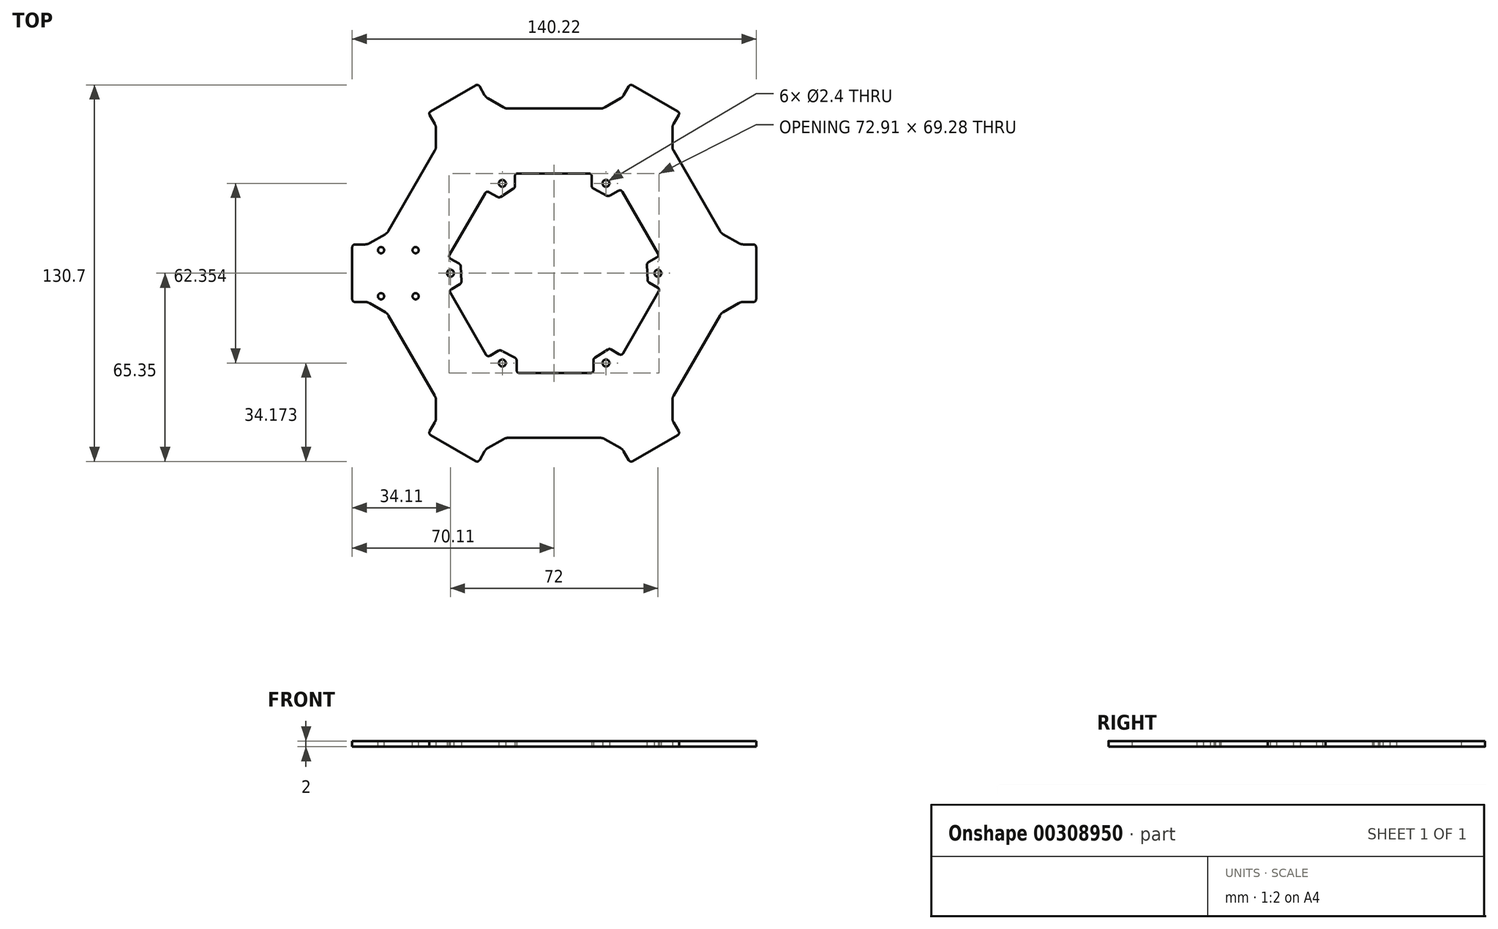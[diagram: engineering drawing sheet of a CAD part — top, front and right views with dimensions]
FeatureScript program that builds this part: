
annotation { "Feature Type Name" : "Feature", "Feature Type Description" : "" }
export const myFeature = defineFeature(function(context is Context, id is Id, definition is map)
    precondition{}
    {
        {
            var Q0;
            Q0=qCreatedBy(makeId("Top.planeOp"),FACE);
            var sketch = newSketch(context, id + "F0", { "sketchPlane" : qUnion([Q0])});
            skPoint(sketch, "E0.0.midPoint", {"position": v(0, 57.16) * mm});
            skLineSegment(sketch, "E1", {"start": v(-16.9, 57.16) * mm, "end": v(-23.73, 61.1) * mm});
            skLineSegment(sketch, "E2", {"start": v(-23.73, 61.1) * mm, "end": v(-26.4, 65.72) * mm});
            skLineSegment(sketch, "E3", {"start": v(-26.4, 65.72) * mm, "end": v(-43.71, 55.72) * mm});
            skLineSegment(sketch, "E4", {"start": v(-43.71, 55.72) * mm, "end": v(-41.05, 51.1) * mm});
            skLineSegment(sketch, "E5", {"start": v(-41.05, 51.1) * mm, "end": v(-41.05, 43.21) * mm});
            skLineSegment(sketch, "E6.1.0", {"start": v(43.71, 55.72) * mm, "end": v(26.4, 65.72) * mm});
            skLineSegment(sketch, "E6.1.1", {"start": v(41.05, 51.1) * mm, "end": v(43.71, 55.72) * mm});
            skLineSegment(sketch, "E6.1.2", {"start": v(41.05, 43.21) * mm, "end": v(41.05, 51.1) * mm});
            skLineSegment(sketch, "E6.1.3", {"start": v(26.4, 65.72) * mm, "end": v(23.73, 61.1) * mm});
            skLineSegment(sketch, "E6.1.4", {"start": v(23.73, 61.1) * mm, "end": v(16.9, 57.16) * mm});
            skLineSegment(sketch, "E6.2.0", {"start": v(70.1, -10) * mm, "end": v(70.1, 10) * mm});
            skLineSegment(sketch, "E6.2.1", {"start": v(64.78, -10) * mm, "end": v(70.1, -10) * mm});
            skLineSegment(sketch, "E6.2.2", {"start": v(57.95, -13.94) * mm, "end": v(64.78, -10) * mm});
            skLineSegment(sketch, "E6.2.3", {"start": v(70.1, 10) * mm, "end": v(64.78, 10) * mm});
            skLineSegment(sketch, "E6.2.4", {"start": v(64.78, 10) * mm, "end": v(57.95, 13.94) * mm});
            skPoint(sketch, "E6.center", {"position": v(0, 0) * mm});
            skLineSegment(sketch, "E7.2.3.0", {"start": v(26.4, -65.72) * mm, "end": v(43.71, -55.72) * mm});
            skLineSegment(sketch, "E7.3.3.0", {"start": v(23.73, -61.1) * mm, "end": v(26.4, -65.72) * mm});
            skLineSegment(sketch, "E7.6.3.0", {"start": v(16.9, -57.16) * mm, "end": v(23.73, -61.1) * mm});
            skLineSegment(sketch, "E7.9.3.0", {"start": v(43.71, -55.72) * mm, "end": v(41.05, -51.1) * mm});
            skLineSegment(sketch, "E7.12.3.0", {"start": v(41.05, -51.1) * mm, "end": v(41.05, -43.21) * mm});
            skLineSegment(sketch, "E7.2.4.0", {"start": v(-43.71, -55.72) * mm, "end": v(-26.4, -65.72) * mm});
            skLineSegment(sketch, "E7.3.4.0", {"start": v(-41.05, -51.1) * mm, "end": v(-43.71, -55.72) * mm});
            skLineSegment(sketch, "E7.6.4.0", {"start": v(-41.05, -43.21) * mm, "end": v(-41.05, -51.1) * mm});
            skLineSegment(sketch, "E7.9.4.0", {"start": v(-26.4, -65.72) * mm, "end": v(-23.73, -61.1) * mm});
            skLineSegment(sketch, "E7.12.4.0", {"start": v(-23.73, -61.1) * mm, "end": v(-16.9, -57.16) * mm});
            skLineSegment(sketch, "E7.2.5.0", {"start": v(-70.1, 10) * mm, "end": v(-70.1, -10) * mm});
            skLineSegment(sketch, "E7.3.5.0", {"start": v(-64.78, 10) * mm, "end": v(-70.1, 10) * mm});
            skLineSegment(sketch, "E7.6.5.0", {"start": v(-57.95, 13.94) * mm, "end": v(-64.78, 10) * mm});
            skLineSegment(sketch, "E7.9.5.0", {"start": v(-70.1, -10) * mm, "end": v(-64.78, -10) * mm});
            skLineSegment(sketch, "E7.12.5.0", {"start": v(-64.78, -10) * mm, "end": v(-57.95, -13.94) * mm});
            skLineSegment(sketch, "E8", {"start": v(16.9, 57.16) * mm, "end": v(-16.9, 57.16) * mm});
            skLineSegment(sketch, "E9", {"start": v(41.05, 43.21) * mm, "end": v(57.95, 13.94) * mm});
            skLineSegment(sketch, "E10", {"start": v(57.95, -13.94) * mm, "end": v(41.05, -43.21) * mm});
            skLineSegment(sketch, "E11", {"start": v(16.9, -57.16) * mm, "end": v(-16.9, -57.16) * mm});
            skLineSegment(sketch, "E12", {"start": v(-41.05, -43.21) * mm, "end": v(-57.95, -13.94) * mm});
            skLineSegment(sketch, "E13", {"start": v(-57.95, 13.94) * mm, "end": v(-41.05, 43.21) * mm});
            skLineSegment(sketch, "E14.0", {"start": v(-20, 34.64) * mm, "end": v(20, 34.64) * mm});
            skLineSegment(sketch, "E14.1", {"start": v(20, 34.64) * mm, "end": v(40, 0) * mm});
            skLineSegment(sketch, "E14.2", {"start": v(40, 0) * mm, "end": v(20, -34.64) * mm});
            skLineSegment(sketch, "E14.3", {"start": v(20, -34.64) * mm, "end": v(-20, -34.64) * mm});
            skLineSegment(sketch, "E14.4", {"start": v(-20, -34.64) * mm, "end": v(-40, 0) * mm});
            skLineSegment(sketch, "E14.5", {"start": v(-40, 0) * mm, "end": v(-20, 34.64) * mm});
            skPoint(sketch, "E14.0.midPoint", {"position": v(0, 34.64) * mm});
            skLineSegment(sketch, "E15", {"start": v(-13.65, 34.64) * mm, "end": v(-13.65, 29.64) * mm});
            skLineSegment(sketch, "E16", {"start": v(-13.65, 29.64) * mm, "end": v(-19.14, 26.13) * mm});
            skLineSegment(sketch, "E17", {"start": v(-19.14, 26.13) * mm, "end": v(-23.47, 28.63) * mm});
            skLineSegment(sketch, "E18.1.0", {"start": v(-32.2, -3.5) * mm, "end": v(-36.53, -6) * mm});
            skLineSegment(sketch, "E18.1.1", {"start": v(-32.5, 3) * mm, "end": v(-32.2, -3.5) * mm});
            skLineSegment(sketch, "E18.1.2", {"start": v(-36.82, 5.5) * mm, "end": v(-32.5, 3) * mm});
            skLineSegment(sketch, "E18.2.0", {"start": v(-13.06, -29.64) * mm, "end": v(-13.06, -34.64) * mm});
            skLineSegment(sketch, "E18.2.1", {"start": v(-18.85, -26.64) * mm, "end": v(-13.06, -29.64) * mm});
            skLineSegment(sketch, "E18.2.2", {"start": v(-23.18, -29.14) * mm, "end": v(-18.85, -26.64) * mm});
            skLineSegment(sketch, "E18.3.0", {"start": v(19.14, -26.13) * mm, "end": v(23.47, -28.63) * mm});
            skLineSegment(sketch, "E18.3.1", {"start": v(13.65, -29.64) * mm, "end": v(19.14, -26.13) * mm});
            skLineSegment(sketch, "E18.3.2", {"start": v(13.65, -34.64) * mm, "end": v(13.65, -29.64) * mm});
            skLineSegment(sketch, "E18.4.0", {"start": v(32.2, 3.5) * mm, "end": v(36.53, 6) * mm});
            skLineSegment(sketch, "E18.4.1", {"start": v(32.5, -3) * mm, "end": v(32.2, 3.5) * mm});
            skLineSegment(sketch, "E18.4.2", {"start": v(36.82, -5.5) * mm, "end": v(32.5, -3) * mm});
            skLineSegment(sketch, "E18.5.0", {"start": v(13.06, 29.64) * mm, "end": v(13.06, 34.64) * mm});
            skLineSegment(sketch, "E18.5.1", {"start": v(18.85, 26.64) * mm, "end": v(13.06, 29.64) * mm});
            skLineSegment(sketch, "E18.5.2", {"start": v(23.18, 29.14) * mm, "end": v(18.85, 26.64) * mm});
            skSolve(sketch);
        }
        {
            var Q0;
            Q0=makeQuery(id+"F0.imprint","IMPRINT",FACE,{"disambiguationData":[TD([[makeQuery(id+"F0.imprint","IMPRINT",EDGE,{"derivedFrom":sQuery(id+"F0.wireOp",EDGE,"E1")}),1.0]])]});
            var Q1;
            {var subQ0=sQuery(id+"F0.wireOp",EDGE,"E15");Q1=makeQuery(id+"F0.imprint","IMPRINT",FACE,{"disambiguationData":[TD([[makeQuery(id+"F0.imprint","IMPRINT",EDGE,{"derivedFrom":subQ0}),-1.0]])]});}
            var Q2;
            {var subQ0=sQuery(id+"F0.wireOp",EDGE,"E18.1.0");Q2=makeQuery(id+"F0.imprint","IMPRINT",FACE,{"disambiguationData":[TD([[makeQuery(id+"F0.imprint","IMPRINT",EDGE,{"derivedFrom":subQ0}),-1.0]])]});}
            var Q3;
            {var subQ0=sQuery(id+"F0.wireOp",EDGE,"E18.5.0");Q3=makeQuery(id+"F0.imprint","IMPRINT",FACE,{"disambiguationData":[TD([[makeQuery(id+"F0.imprint","IMPRINT",EDGE,{"derivedFrom":subQ0}),-1.0]])]});}
            var Q4;
            {var subQ4=sQuery(id+"F0.wireOp",EDGE,"E18.4.0");Q4=makeQuery(id+"F0.imprint","IMPRINT",FACE,{"disambiguationData":[TD([[makeQuery(id+"F0.imprint","IMPRINT",EDGE,{"derivedFrom":subQ4}),-1.0]])]});}
            var Q5;
            {var subQ0=sQuery(id+"F0.wireOp",EDGE,"E18.3.0");Q5=makeQuery(id+"F0.imprint","IMPRINT",FACE,{"disambiguationData":[TD([[makeQuery(id+"F0.imprint","IMPRINT",EDGE,{"derivedFrom":subQ0}),-1.0]])]});}
            var Q6;
            {var subQ0=sQuery(id+"F0.wireOp",EDGE,"E18.2.0");Q6=makeQuery(id+"F0.imprint","IMPRINT",FACE,{"disambiguationData":[TD([[makeQuery(id+"F0.imprint","IMPRINT",EDGE,{"derivedFrom":subQ0}),-1.0]])]});}
            extrude(context, id + "F1", {"entities" : qUnion([Q0, Q1, Q2, Q3, Q4, Q5, Q6]), "offsetDistance" : 25 * mm, "depth" : 2 * mm});
        }
        {
            var Q0;
            Q0=qCreatedBy(makeId("Top.planeOp"),FACE);
            var sketch = newSketch(context, id + "F2", { "sketchPlane" : qUnion([Q0])});
            skCircle(sketch, "E19.cCircle", {"center": v(0, 0) * mm, "radius": 31.18 * mm, "construction": true});
            skLineSegment(sketch, "E19.0", {"start": v(-18, 31.18) * mm, "end": v(18, 31.18) * mm});
            skLineSegment(sketch, "E19.1", {"start": v(18, 31.18) * mm, "end": v(36, 0) * mm});
            skLineSegment(sketch, "E19.2", {"start": v(36, 0) * mm, "end": v(18, -31.18) * mm});
            skLineSegment(sketch, "E19.3", {"start": v(18, -31.18) * mm, "end": v(-18, -31.18) * mm});
            skLineSegment(sketch, "E19.4", {"start": v(-18, -31.18) * mm, "end": v(-36, 0) * mm});
            skLineSegment(sketch, "E19.5", {"start": v(-36, 0) * mm, "end": v(-18, 31.18) * mm});
            skPoint(sketch, "E19.0.midPoint", {"position": v(0, 31.18) * mm});
            skSolve(sketch);
        }
        {
            var Q0;
            Q0=sQuery(id+"F2.wireOp",VERTEX,"E19.5.start");
            var Q1;
            Q1=sQuery(id+"F2.wireOp",VERTEX,"E19.0.start");
            var Q2;
            Q2=sQuery(id+"F2.wireOp",VERTEX,"E19.1.start");
            var Q3;
            Q3=sQuery(id+"F2.wireOp",VERTEX,"E19.2.start");
            var Q4;
            Q4=sQuery(id+"F2.wireOp",VERTEX,"E19.3.start");
            var Q5;
            Q5=sQuery(id+"F2.wireOp",VERTEX,"E19.4.start");
            var Q6;
            Q6=makeQuery(id+"F1.opExtrude","SWEPT_BODY",BODY,{"disambiguationData":[OSD([sQuery(id+"F0.wireOp",EDGE,"E1"),sQuery(id+"F0.wireOp",EDGE,"E2"),sQuery(id+"F0.wireOp",EDGE,"E3"),sQuery(id+"F0.wireOp",EDGE,"E4"),sQuery(id+"F0.wireOp",EDGE,"E5"),sQuery(id+"F0.wireOp",EDGE,"E6.1.0"),sQuery(id+"F0.wireOp",EDGE,"E6.1.1"),sQuery(id+"F0.wireOp",EDGE,"E6.1.2"),sQuery(id+"F0.wireOp",EDGE,"E6.1.3"),sQuery(id+"F0.wireOp",EDGE,"E6.1.4"),sQuery(id+"F0.wireOp",EDGE,"E6.2.0"),sQuery(id+"F0.wireOp",EDGE,"E6.2.1"),sQuery(id+"F0.wireOp",EDGE,"E6.2.2"),sQuery(id+"F0.wireOp",EDGE,"E6.2.3"),sQuery(id+"F0.wireOp",EDGE,"E6.2.4"),sQuery(id+"F0.wireOp",EDGE,"E7.2.3.0"),sQuery(id+"F0.wireOp",EDGE,"E7.3.3.0"),sQuery(id+"F0.wireOp",EDGE,"E7.6.3.0"),sQuery(id+"F0.wireOp",EDGE,"E7.9.3.0"),sQuery(id+"F0.wireOp",EDGE,"E7.12.3.0"),sQuery(id+"F0.wireOp",EDGE,"E7.2.4.0"),sQuery(id+"F0.wireOp",EDGE,"E7.3.4.0"),sQuery(id+"F0.wireOp",EDGE,"E7.6.4.0"),sQuery(id+"F0.wireOp",EDGE,"E7.9.4.0"),sQuery(id+"F0.wireOp",EDGE,"E7.12.4.0"),sQuery(id+"F0.wireOp",EDGE,"E7.2.5.0"),sQuery(id+"F0.wireOp",EDGE,"E7.3.5.0"),sQuery(id+"F0.wireOp",EDGE,"E7.6.5.0"),sQuery(id+"F0.wireOp",EDGE,"E7.9.5.0"),sQuery(id+"F0.wireOp",EDGE,"E7.12.5.0"),sQuery(id+"F0.wireOp",EDGE,"E8"),sQuery(id+"F0.wireOp",EDGE,"E9"),sQuery(id+"F0.wireOp",EDGE,"E10"),sQuery(id+"F0.wireOp",EDGE,"E11"),sQuery(id+"F0.wireOp",EDGE,"E12"),sQuery(id+"F0.wireOp",EDGE,"E13"),sQuery(id+"F0.wireOp",EDGE,"E14.0"),sQuery(id+"F0.wireOp",EDGE,"E14.1"),sQuery(id+"F0.wireOp",EDGE,"E14.2"),sQuery(id+"F0.wireOp",EDGE,"E14.3"),sQuery(id+"F0.wireOp",EDGE,"E14.4"),sQuery(id+"F0.wireOp",EDGE,"E14.5"),sQuery(id+"F0.wireOp",EDGE,"E15"),sQuery(id+"F0.wireOp",EDGE,"E16"),sQuery(id+"F0.wireOp",EDGE,"E17"),sQuery(id+"F0.wireOp",EDGE,"E18.1.0"),sQuery(id+"F0.wireOp",EDGE,"E18.1.1"),sQuery(id+"F0.wireOp",EDGE,"E18.1.2"),sQuery(id+"F0.wireOp",EDGE,"E18.2.0"),sQuery(id+"F0.wireOp",EDGE,"E18.2.1"),sQuery(id+"F0.wireOp",EDGE,"E18.2.2"),sQuery(id+"F0.wireOp",EDGE,"E18.3.0"),sQuery(id+"F0.wireOp",EDGE,"E18.3.1"),sQuery(id+"F0.wireOp",EDGE,"E18.3.2"),sQuery(id+"F0.wireOp",EDGE,"E18.4.0"),sQuery(id+"F0.wireOp",EDGE,"E18.4.1"),sQuery(id+"F0.wireOp",EDGE,"E18.4.2"),sQuery(id+"F0.wireOp",EDGE,"E18.5.0"),sQuery(id+"F0.wireOp",EDGE,"E18.5.1"),sQuery(id+"F0.wireOp",EDGE,"E18.5.2")])]});
            hole(context, id + "F3", {"style" : HoleStyle.SIMPLE, "endStyle" : HoleEndStyle.THROUGH, "oppositeDirection" : true, "standardTappedOrClearance" : lookupTablePath({ "standard" : "ISO", "engagement" : "75%", "pitch" : "0.6 mm", "size" : "M3", "type" : "Tapped" }), "standardBlindInLast" : lookupTablePath({ "standard" : "ISO", "engagement" : "75%", "pitch" : "0.6 mm", "size" : "M3", "type" : "Tapped" }), "holeDiameter" : 2.4 * mm, "majorDiameter" : 5 * mm, "showTappedDepth" : true, "tappedDepth" : 12 * mm, "tapClearance" : 3, "locations" : qUnion([Q0, Q1, Q2, Q3, Q4, Q5]), "scope" : qUnion([Q6])});
        }
        {
            var Q0;
            Q0=makeQuery(id+"F1.opExtrude","SWEPT_EDGE",EDGE,{"disambiguationData":[OSD([sQuery(id+"F0.wireOp",EDGE,"E7.2.4.0"),sQuery(id+"F0.wireOp",EDGE,"E7.9.4.0")])]});
            var Q1;
            Q1=makeQuery(id+"F1.opExtrude","SWEPT_EDGE",EDGE,{"disambiguationData":[OSD([sQuery(id+"F0.wireOp",EDGE,"E7.2.4.0"),sQuery(id+"F0.wireOp",EDGE,"E7.3.4.0")])]});
            var Q2;
            Q2=makeQuery(id+"F1.opExtrude","SWEPT_EDGE",EDGE,{"disambiguationData":[OSD([sQuery(id+"F0.wireOp",EDGE,"E7.2.3.0"),sQuery(id+"F0.wireOp",EDGE,"E7.3.3.0")])]});
            var Q3;
            Q3=makeQuery(id+"F1.opExtrude","SWEPT_EDGE",EDGE,{"disambiguationData":[OSD([sQuery(id+"F0.wireOp",EDGE,"E7.2.3.0"),sQuery(id+"F0.wireOp",EDGE,"E7.9.3.0")])]});
            var Q4;
            Q4=makeQuery(id+"F1.opExtrude","SWEPT_EDGE",EDGE,{"disambiguationData":[OSD([sQuery(id+"F0.wireOp",EDGE,"E6.2.0"),sQuery(id+"F0.wireOp",EDGE,"E6.2.1")])]});
            var Q5;
            Q5=makeQuery(id+"F1.opExtrude","SWEPT_EDGE",EDGE,{"disambiguationData":[OSD([sQuery(id+"F0.wireOp",EDGE,"E6.2.0"),sQuery(id+"F0.wireOp",EDGE,"E6.2.3")])]});
            var Q6;
            Q6=makeQuery(id+"F1.opExtrude","SWEPT_EDGE",EDGE,{"disambiguationData":[OSD([sQuery(id+"F0.wireOp",EDGE,"E6.1.0"),sQuery(id+"F0.wireOp",EDGE,"E6.1.3")])]});
            var Q7;
            Q7=makeQuery(id+"F1.opExtrude","SWEPT_EDGE",EDGE,{"disambiguationData":[OSD([sQuery(id+"F0.wireOp",EDGE,"E6.1.0"),sQuery(id+"F0.wireOp",EDGE,"E6.1.1")])]});
            var Q8;
            Q8=makeQuery(id+"F1.opExtrude","SWEPT_EDGE",EDGE,{"disambiguationData":[OSD([sQuery(id+"F0.wireOp",EDGE,"E2"),sQuery(id+"F0.wireOp",EDGE,"E3")])]});
            var Q9;
            Q9=makeQuery(id+"F1.opExtrude","SWEPT_EDGE",EDGE,{"disambiguationData":[OSD([sQuery(id+"F0.wireOp",EDGE,"E3"),sQuery(id+"F0.wireOp",EDGE,"E4")])]});
            var Q10;
            Q10=makeQuery(id+"F1.opExtrude","SWEPT_EDGE",EDGE,{"disambiguationData":[OSD([sQuery(id+"F0.wireOp",EDGE,"E7.2.5.0"),sQuery(id+"F0.wireOp",EDGE,"E7.3.5.0")])]});
            var Q11;
            Q11=makeQuery(id+"F1.opExtrude","SWEPT_EDGE",EDGE,{"disambiguationData":[OSD([sQuery(id+"F0.wireOp",EDGE,"E7.2.5.0"),sQuery(id+"F0.wireOp",EDGE,"E7.9.5.0")])]});
            var Q12;
            Q12=makeQuery(id+"F1.opExtrude","SWEPT_EDGE",EDGE,{"disambiguationData":[OSD([sQuery(id+"F0.wireOp",EDGE,"E18.4.0"),sQuery(id+"F0.wireOp",EDGE,"E18.4.1")])]});
            var Q13;
            Q13=makeQuery(id+"F1.opExtrude","SWEPT_EDGE",EDGE,{"disambiguationData":[OSD([sQuery(id+"F0.wireOp",EDGE,"E18.4.1"),sQuery(id+"F0.wireOp",EDGE,"E18.4.2")])]});
            var Q14;
            Q14=makeQuery(id+"F1.opExtrude","SWEPT_EDGE",EDGE,{"disambiguationData":[OSD([sQuery(id+"F0.wireOp",EDGE,"E18.3.1"),sQuery(id+"F0.wireOp",EDGE,"E18.3.2")])]});
            var Q15;
            Q15=makeQuery(id+"F1.opExtrude","SWEPT_EDGE",EDGE,{"disambiguationData":[OSD([sQuery(id+"F0.wireOp",EDGE,"E18.3.0"),sQuery(id+"F0.wireOp",EDGE,"E18.3.1")])]});
            var Q16;
            Q16=makeQuery(id+"F1.opExtrude","SWEPT_EDGE",EDGE,{"disambiguationData":[OSD([sQuery(id+"F0.wireOp",EDGE,"E18.2.1"),sQuery(id+"F0.wireOp",EDGE,"E18.2.2")])]});
            var Q17;
            Q17=makeQuery(id+"F1.opExtrude","SWEPT_EDGE",EDGE,{"disambiguationData":[OSD([sQuery(id+"F0.wireOp",EDGE,"E18.2.0"),sQuery(id+"F0.wireOp",EDGE,"E18.2.1")])]});
            var Q18;
            Q18=makeQuery(id+"F1.opExtrude","SWEPT_EDGE",EDGE,{"disambiguationData":[OSD([sQuery(id+"F0.wireOp",EDGE,"E18.1.1"),sQuery(id+"F0.wireOp",EDGE,"E18.1.2")])]});
            var Q19;
            Q19=makeQuery(id+"F1.opExtrude","SWEPT_EDGE",EDGE,{"disambiguationData":[OSD([sQuery(id+"F0.wireOp",EDGE,"E18.1.0"),sQuery(id+"F0.wireOp",EDGE,"E18.1.1")])]});
            var Q20;
            Q20=makeQuery(id+"F1.opExtrude","SWEPT_EDGE",EDGE,{"disambiguationData":[OSD([sQuery(id+"F0.wireOp",EDGE,"E16"),sQuery(id+"F0.wireOp",EDGE,"E17")])]});
            var Q21;
            Q21=makeQuery(id+"F1.opExtrude","SWEPT_EDGE",EDGE,{"disambiguationData":[OSD([sQuery(id+"F0.wireOp",EDGE,"E15"),sQuery(id+"F0.wireOp",EDGE,"E16")])]});
            var Q22;
            Q22=makeQuery(id+"F1.opExtrude","SWEPT_EDGE",EDGE,{"disambiguationData":[OSD([sQuery(id+"F0.wireOp",EDGE,"E18.5.0"),sQuery(id+"F0.wireOp",EDGE,"E18.5.1")])]});
            var Q23;
            Q23=makeQuery(id+"F1.opExtrude","SWEPT_EDGE",EDGE,{"disambiguationData":[OSD([sQuery(id+"F0.wireOp",EDGE,"E18.5.1"),sQuery(id+"F0.wireOp",EDGE,"E18.5.2")])]});
            var Q24;
            Q24=makeQuery(id+"F1.opExtrude","SWEPT_EDGE",EDGE,{"disambiguationData":[OSD([sQuery(id+"F0.wireOp",EDGE,"E14.1"),sQuery(id+"F0.wireOp",EDGE,"E18.5.2")])]});
            var Q25;
            Q25=makeQuery(id+"F1.opExtrude","SWEPT_EDGE",EDGE,{"disambiguationData":[OSD([sQuery(id+"F0.wireOp",EDGE,"E14.0"),sQuery(id+"F0.wireOp",EDGE,"E18.5.0")])]});
            var Q26;
            Q26=makeQuery(id+"F1.opExtrude","SWEPT_EDGE",EDGE,{"disambiguationData":[OSD([sQuery(id+"F0.wireOp",EDGE,"E14.2"),sQuery(id+"F0.wireOp",EDGE,"E18.4.2")])]});
            var Q27;
            Q27=makeQuery(id+"F1.opExtrude","SWEPT_EDGE",EDGE,{"disambiguationData":[OSD([sQuery(id+"F0.wireOp",EDGE,"E14.1"),sQuery(id+"F0.wireOp",EDGE,"E18.4.0")])]});
            var Q28;
            Q28=makeQuery(id+"F1.opExtrude","SWEPT_EDGE",EDGE,{"disambiguationData":[OSD([sQuery(id+"F0.wireOp",EDGE,"E14.2"),sQuery(id+"F0.wireOp",EDGE,"E18.3.0")])]});
            var Q29;
            Q29=makeQuery(id+"F1.opExtrude","SWEPT_EDGE",EDGE,{"disambiguationData":[OSD([sQuery(id+"F0.wireOp",EDGE,"E14.3"),sQuery(id+"F0.wireOp",EDGE,"E18.3.2")])]});
            var Q30;
            Q30=makeQuery(id+"F1.opExtrude","SWEPT_EDGE",EDGE,{"disambiguationData":[OSD([sQuery(id+"F0.wireOp",EDGE,"E14.3"),sQuery(id+"F0.wireOp",EDGE,"E18.2.0")])]});
            var Q31;
            Q31=makeQuery(id+"F1.opExtrude","SWEPT_EDGE",EDGE,{"disambiguationData":[OSD([sQuery(id+"F0.wireOp",EDGE,"E14.5"),sQuery(id+"F0.wireOp",EDGE,"E18.1.2")])]});
            var Q32;
            Q32=makeQuery(id+"F1.opExtrude","SWEPT_EDGE",EDGE,{"disambiguationData":[OSD([sQuery(id+"F0.wireOp",EDGE,"E14.4"),sQuery(id+"F0.wireOp",EDGE,"E18.1.0")])]});
            var Q33;
            Q33=makeQuery(id+"F1.opExtrude","SWEPT_EDGE",EDGE,{"disambiguationData":[OSD([sQuery(id+"F0.wireOp",EDGE,"E14.4"),sQuery(id+"F0.wireOp",EDGE,"E18.2.2")])]});
            var Q34;
            Q34=makeQuery(id+"F1.opExtrude","SWEPT_EDGE",EDGE,{"disambiguationData":[OSD([sQuery(id+"F0.wireOp",EDGE,"E14.0"),sQuery(id+"F0.wireOp",EDGE,"E15")])]});
            var Q35;
            Q35=makeQuery(id+"F1.opExtrude","SWEPT_EDGE",EDGE,{"disambiguationData":[OSD([sQuery(id+"F0.wireOp",EDGE,"E14.5"),sQuery(id+"F0.wireOp",EDGE,"E17")])]});
            fillet(context, id + "F4", {"entities" : qUnion([Q0, Q1, Q2, Q3, Q4, Q5, Q6, Q7, Q8, Q9, Q10, Q11, Q12, Q13, Q14, Q15, Q16, Q17, Q18, Q19, Q20, Q21, Q22, Q23, Q24, Q25, Q26, Q27, Q28, Q29, Q30, Q31, Q32, Q33, Q34, Q35]), "radius" : 1 * mm, "tangentPropagation" : true, "allowEdgeOverflow" : false});
        }
        {
            var Q0;
            Q0=makeQuery(id+"F1.opExtrude","SWEPT_EDGE",EDGE,{"disambiguationData":[OSD([sQuery(id+"F0.wireOp",EDGE,"E7.9.5.0"),sQuery(id+"F0.wireOp",EDGE,"E7.12.5.0")])]});
            var Q1;
            Q1=makeQuery(id+"F1.opExtrude","SWEPT_EDGE",EDGE,{"disambiguationData":[OSD([sQuery(id+"F0.wireOp",EDGE,"E7.12.5.0"),sQuery(id+"F0.wireOp",EDGE,"E12")])]});
            var Q2;
            Q2=makeQuery(id+"F1.opExtrude","SWEPT_EDGE",EDGE,{"disambiguationData":[OSD([sQuery(id+"F0.wireOp",EDGE,"E7.6.4.0"),sQuery(id+"F0.wireOp",EDGE,"E12")])]});
            var Q3;
            Q3=makeQuery(id+"F1.opExtrude","SWEPT_EDGE",EDGE,{"disambiguationData":[OSD([sQuery(id+"F0.wireOp",EDGE,"E7.3.4.0"),sQuery(id+"F0.wireOp",EDGE,"E7.6.4.0")])]});
            var Q4;
            Q4=makeQuery(id+"F1.opExtrude","SWEPT_EDGE",EDGE,{"disambiguationData":[OSD([sQuery(id+"F0.wireOp",EDGE,"E7.12.4.0"),sQuery(id+"F0.wireOp",EDGE,"E11")])]});
            var Q5;
            Q5=makeQuery(id+"F1.opExtrude","SWEPT_EDGE",EDGE,{"disambiguationData":[OSD([sQuery(id+"F0.wireOp",EDGE,"E7.9.4.0"),sQuery(id+"F0.wireOp",EDGE,"E7.12.4.0")])]});
            var Q6;
            Q6=makeQuery(id+"F1.opExtrude","SWEPT_EDGE",EDGE,{"disambiguationData":[OSD([sQuery(id+"F0.wireOp",EDGE,"E7.6.3.0"),sQuery(id+"F0.wireOp",EDGE,"E11")])]});
            var Q7;
            Q7=makeQuery(id+"F1.opExtrude","SWEPT_EDGE",EDGE,{"disambiguationData":[OSD([sQuery(id+"F0.wireOp",EDGE,"E7.3.3.0"),sQuery(id+"F0.wireOp",EDGE,"E7.6.3.0")])]});
            var Q8;
            Q8=makeQuery(id+"F1.opExtrude","SWEPT_EDGE",EDGE,{"disambiguationData":[OSD([sQuery(id+"F0.wireOp",EDGE,"E7.9.3.0"),sQuery(id+"F0.wireOp",EDGE,"E7.12.3.0")])]});
            var Q9;
            Q9=makeQuery(id+"F1.opExtrude","SWEPT_EDGE",EDGE,{"disambiguationData":[OSD([sQuery(id+"F0.wireOp",EDGE,"E7.12.3.0"),sQuery(id+"F0.wireOp",EDGE,"E10")])]});
            var Q10;
            Q10=makeQuery(id+"F1.opExtrude","SWEPT_EDGE",EDGE,{"disambiguationData":[OSD([sQuery(id+"F0.wireOp",EDGE,"E6.2.2"),sQuery(id+"F0.wireOp",EDGE,"E10")])]});
            var Q11;
            Q11=makeQuery(id+"F1.opExtrude","SWEPT_EDGE",EDGE,{"disambiguationData":[OSD([sQuery(id+"F0.wireOp",EDGE,"E6.2.1"),sQuery(id+"F0.wireOp",EDGE,"E6.2.2")])]});
            var Q12;
            Q12=makeQuery(id+"F1.opExtrude","SWEPT_EDGE",EDGE,{"disambiguationData":[OSD([sQuery(id+"F0.wireOp",EDGE,"E6.2.4"),sQuery(id+"F0.wireOp",EDGE,"E9")])]});
            var Q13;
            Q13=makeQuery(id+"F1.opExtrude","SWEPT_EDGE",EDGE,{"disambiguationData":[OSD([sQuery(id+"F0.wireOp",EDGE,"E6.2.3"),sQuery(id+"F0.wireOp",EDGE,"E6.2.4")])]});
            var Q14;
            Q14=makeQuery(id+"F1.opExtrude","SWEPT_EDGE",EDGE,{"disambiguationData":[OSD([sQuery(id+"F0.wireOp",EDGE,"E6.1.1"),sQuery(id+"F0.wireOp",EDGE,"E6.1.2")])]});
            var Q15;
            Q15=makeQuery(id+"F1.opExtrude","SWEPT_EDGE",EDGE,{"disambiguationData":[OSD([sQuery(id+"F0.wireOp",EDGE,"E6.1.2"),sQuery(id+"F0.wireOp",EDGE,"E9")])]});
            var Q16;
            Q16=makeQuery(id+"F1.opExtrude","SWEPT_EDGE",EDGE,{"disambiguationData":[OSD([sQuery(id+"F0.wireOp",EDGE,"E6.1.3"),sQuery(id+"F0.wireOp",EDGE,"E6.1.4")])]});
            var Q17;
            Q17=makeQuery(id+"F1.opExtrude","SWEPT_EDGE",EDGE,{"disambiguationData":[OSD([sQuery(id+"F0.wireOp",EDGE,"E6.1.4"),sQuery(id+"F0.wireOp",EDGE,"E8")])]});
            var Q18;
            Q18=makeQuery(id+"F1.opExtrude","SWEPT_EDGE",EDGE,{"disambiguationData":[OSD([sQuery(id+"F0.wireOp",EDGE,"E1"),sQuery(id+"F0.wireOp",EDGE,"E8")])]});
            var Q19;
            Q19=makeQuery(id+"F1.opExtrude","SWEPT_EDGE",EDGE,{"disambiguationData":[OSD([sQuery(id+"F0.wireOp",EDGE,"E1"),sQuery(id+"F0.wireOp",EDGE,"E2")])]});
            var Q20;
            Q20=makeQuery(id+"F1.opExtrude","SWEPT_EDGE",EDGE,{"disambiguationData":[OSD([sQuery(id+"F0.wireOp",EDGE,"E5"),sQuery(id+"F0.wireOp",EDGE,"E13")])]});
            var Q21;
            Q21=makeQuery(id+"F1.opExtrude","SWEPT_EDGE",EDGE,{"disambiguationData":[OSD([sQuery(id+"F0.wireOp",EDGE,"E4"),sQuery(id+"F0.wireOp",EDGE,"E5")])]});
            var Q22;
            Q22=makeQuery(id+"F1.opExtrude","SWEPT_EDGE",EDGE,{"disambiguationData":[OSD([sQuery(id+"F0.wireOp",EDGE,"E7.3.5.0"),sQuery(id+"F0.wireOp",EDGE,"E7.6.5.0")])]});
            var Q23;
            Q23=makeQuery(id+"F1.opExtrude","SWEPT_EDGE",EDGE,{"disambiguationData":[OSD([sQuery(id+"F0.wireOp",EDGE,"E7.6.5.0"),sQuery(id+"F0.wireOp",EDGE,"E13")])]});
            fillet(context, id + "F5", {"entities" : qUnion([Q0, Q1, Q2, Q3, Q4, Q5, Q6, Q7, Q8, Q9, Q10, Q11, Q12, Q13, Q14, Q15, Q16, Q17, Q18, Q19, Q20, Q21, Q22, Q23]), "radius" : 3 * mm, "tangentPropagation" : true, "allowEdgeOverflow" : false});
        }
        {
            var Q0;
            Q0=makeQuery(id+"F1.opExtrude","CAP_FACE",FACE,{"disambiguationData":[OSD([sQuery(id+"F0.wireOp",EDGE,"E1"),sQuery(id+"F0.wireOp",EDGE,"E2"),sQuery(id+"F0.wireOp",EDGE,"E3"),sQuery(id+"F0.wireOp",EDGE,"E4"),sQuery(id+"F0.wireOp",EDGE,"E5"),sQuery(id+"F0.wireOp",EDGE,"E6.1.0"),sQuery(id+"F0.wireOp",EDGE,"E6.1.1"),sQuery(id+"F0.wireOp",EDGE,"E6.1.2"),sQuery(id+"F0.wireOp",EDGE,"E6.1.3"),sQuery(id+"F0.wireOp",EDGE,"E6.1.4"),sQuery(id+"F0.wireOp",EDGE,"E6.2.0"),sQuery(id+"F0.wireOp",EDGE,"E6.2.1"),sQuery(id+"F0.wireOp",EDGE,"E6.2.2"),sQuery(id+"F0.wireOp",EDGE,"E6.2.3"),sQuery(id+"F0.wireOp",EDGE,"E6.2.4"),sQuery(id+"F0.wireOp",EDGE,"E7.2.3.0"),sQuery(id+"F0.wireOp",EDGE,"E7.3.3.0"),sQuery(id+"F0.wireOp",EDGE,"E7.6.3.0"),sQuery(id+"F0.wireOp",EDGE,"E7.9.3.0"),sQuery(id+"F0.wireOp",EDGE,"E7.12.3.0"),sQuery(id+"F0.wireOp",EDGE,"E7.2.4.0"),sQuery(id+"F0.wireOp",EDGE,"E7.3.4.0"),sQuery(id+"F0.wireOp",EDGE,"E7.6.4.0"),sQuery(id+"F0.wireOp",EDGE,"E7.9.4.0"),sQuery(id+"F0.wireOp",EDGE,"E7.12.4.0"),sQuery(id+"F0.wireOp",EDGE,"E7.2.5.0"),sQuery(id+"F0.wireOp",EDGE,"E7.3.5.0"),sQuery(id+"F0.wireOp",EDGE,"E7.6.5.0"),sQuery(id+"F0.wireOp",EDGE,"E7.9.5.0"),sQuery(id+"F0.wireOp",EDGE,"E7.12.5.0"),sQuery(id+"F0.wireOp",EDGE,"E8"),sQuery(id+"F0.wireOp",EDGE,"E9"),sQuery(id+"F0.wireOp",EDGE,"E10"),sQuery(id+"F0.wireOp",EDGE,"E11"),sQuery(id+"F0.wireOp",EDGE,"E12"),sQuery(id+"F0.wireOp",EDGE,"E13"),sQuery(id+"F0.wireOp",EDGE,"E14.0"),sQuery(id+"F0.wireOp",EDGE,"E14.1"),sQuery(id+"F0.wireOp",EDGE,"E14.2"),sQuery(id+"F0.wireOp",EDGE,"E14.3"),sQuery(id+"F0.wireOp",EDGE,"E14.4"),sQuery(id+"F0.wireOp",EDGE,"E14.5"),sQuery(id+"F0.wireOp",EDGE,"E15"),sQuery(id+"F0.wireOp",EDGE,"E16"),sQuery(id+"F0.wireOp",EDGE,"E17"),sQuery(id+"F0.wireOp",EDGE,"E18.1.0"),sQuery(id+"F0.wireOp",EDGE,"E18.1.1"),sQuery(id+"F0.wireOp",EDGE,"E18.1.2"),sQuery(id+"F0.wireOp",EDGE,"E18.2.0"),sQuery(id+"F0.wireOp",EDGE,"E18.2.1"),sQuery(id+"F0.wireOp",EDGE,"E18.2.2"),sQuery(id+"F0.wireOp",EDGE,"E18.3.0"),sQuery(id+"F0.wireOp",EDGE,"E18.3.1"),sQuery(id+"F0.wireOp",EDGE,"E18.3.2"),sQuery(id+"F0.wireOp",EDGE,"E18.4.0"),sQuery(id+"F0.wireOp",EDGE,"E18.4.1"),sQuery(id+"F0.wireOp",EDGE,"E18.4.2"),sQuery(id+"F0.wireOp",EDGE,"E18.5.0"),sQuery(id+"F0.wireOp",EDGE,"E18.5.1"),sQuery(id+"F0.wireOp",EDGE,"E18.5.2")])],"isStart":false});
            var sketch = newSketch(context, id + "F6", { "sketchPlane" : qUnion([Q0])});
            skLineSegment(sketch, "E20", {"start": v(-60.1, 8) * mm, "end": v(-60.1, -8) * mm});
            skLineSegment(sketch, "E21", {"start": v(-48.1, 8) * mm, "end": v(-48.1, -8) * mm});
            skSolve(sketch);
        }
        {
            var Q0;
            Q0=sQuery(id+"F6.wireOp",VERTEX,"E21.start");
            var Q1;
            Q1=sQuery(id+"F6.wireOp",VERTEX,"E21.end");
            var Q2;
            Q2=sQuery(id+"F6.wireOp",VERTEX,"E20.end");
            var Q3;
            Q3=sQuery(id+"F6.wireOp",VERTEX,"E20.start");
            var Q4;
            Q4=makeQuery(id+"F1.opExtrude","SWEPT_BODY",BODY,{"disambiguationData":[OSD([sQuery(id+"F0.wireOp",EDGE,"E1"),sQuery(id+"F0.wireOp",EDGE,"E2"),sQuery(id+"F0.wireOp",EDGE,"E3"),sQuery(id+"F0.wireOp",EDGE,"E4"),sQuery(id+"F0.wireOp",EDGE,"E5"),sQuery(id+"F0.wireOp",EDGE,"E6.1.0"),sQuery(id+"F0.wireOp",EDGE,"E6.1.1"),sQuery(id+"F0.wireOp",EDGE,"E6.1.2"),sQuery(id+"F0.wireOp",EDGE,"E6.1.3"),sQuery(id+"F0.wireOp",EDGE,"E6.1.4"),sQuery(id+"F0.wireOp",EDGE,"E6.2.0"),sQuery(id+"F0.wireOp",EDGE,"E6.2.1"),sQuery(id+"F0.wireOp",EDGE,"E6.2.2"),sQuery(id+"F0.wireOp",EDGE,"E6.2.3"),sQuery(id+"F0.wireOp",EDGE,"E6.2.4"),sQuery(id+"F0.wireOp",EDGE,"E7.2.3.0"),sQuery(id+"F0.wireOp",EDGE,"E7.3.3.0"),sQuery(id+"F0.wireOp",EDGE,"E7.6.3.0"),sQuery(id+"F0.wireOp",EDGE,"E7.9.3.0"),sQuery(id+"F0.wireOp",EDGE,"E7.12.3.0"),sQuery(id+"F0.wireOp",EDGE,"E7.2.4.0"),sQuery(id+"F0.wireOp",EDGE,"E7.3.4.0"),sQuery(id+"F0.wireOp",EDGE,"E7.6.4.0"),sQuery(id+"F0.wireOp",EDGE,"E7.9.4.0"),sQuery(id+"F0.wireOp",EDGE,"E7.12.4.0"),sQuery(id+"F0.wireOp",EDGE,"E7.2.5.0"),sQuery(id+"F0.wireOp",EDGE,"E7.3.5.0"),sQuery(id+"F0.wireOp",EDGE,"E7.6.5.0"),sQuery(id+"F0.wireOp",EDGE,"E7.9.5.0"),sQuery(id+"F0.wireOp",EDGE,"E7.12.5.0"),sQuery(id+"F0.wireOp",EDGE,"E8"),sQuery(id+"F0.wireOp",EDGE,"E9"),sQuery(id+"F0.wireOp",EDGE,"E10"),sQuery(id+"F0.wireOp",EDGE,"E11"),sQuery(id+"F0.wireOp",EDGE,"E12"),sQuery(id+"F0.wireOp",EDGE,"E13"),sQuery(id+"F0.wireOp",EDGE,"E14.0"),sQuery(id+"F0.wireOp",EDGE,"E14.1"),sQuery(id+"F0.wireOp",EDGE,"E14.2"),sQuery(id+"F0.wireOp",EDGE,"E14.3"),sQuery(id+"F0.wireOp",EDGE,"E14.4"),sQuery(id+"F0.wireOp",EDGE,"E14.5"),sQuery(id+"F0.wireOp",EDGE,"E15"),sQuery(id+"F0.wireOp",EDGE,"E16"),sQuery(id+"F0.wireOp",EDGE,"E17"),sQuery(id+"F0.wireOp",EDGE,"E18.1.0"),sQuery(id+"F0.wireOp",EDGE,"E18.1.1"),sQuery(id+"F0.wireOp",EDGE,"E18.1.2"),sQuery(id+"F0.wireOp",EDGE,"E18.2.0"),sQuery(id+"F0.wireOp",EDGE,"E18.2.1"),sQuery(id+"F0.wireOp",EDGE,"E18.2.2"),sQuery(id+"F0.wireOp",EDGE,"E18.3.0"),sQuery(id+"F0.wireOp",EDGE,"E18.3.1"),sQuery(id+"F0.wireOp",EDGE,"E18.3.2"),sQuery(id+"F0.wireOp",EDGE,"E18.4.0"),sQuery(id+"F0.wireOp",EDGE,"E18.4.1"),sQuery(id+"F0.wireOp",EDGE,"E18.4.2"),sQuery(id+"F0.wireOp",EDGE,"E18.5.0"),sQuery(id+"F0.wireOp",EDGE,"E18.5.1"),sQuery(id+"F0.wireOp",EDGE,"E18.5.2")])]});
            hole(context, id + "F7", {"style" : HoleStyle.SIMPLE, "endStyle" : HoleEndStyle.THROUGH, "standardTappedOrClearance" : lookupTablePath({ "standard" : "ISO", "engagement" : "75%", "pitch" : "0.35 mm", "size" : "M2.5", "type" : "Tapped" }), "standardBlindInLast" : lookupTablePath({ "standard" : "ISO", "fit" : "Normal", "engagement" : "75%", "pitch" : "0.35 mm", "size" : "M2.5", "type" : "Clearance & tapped" }), "holeDiameter" : 2.15 * mm, "majorDiameter" : 2.5 * mm, "showTappedDepth" : true, "tappedDepth" : 12 * mm, "tapClearance" : 3, "locations" : qUnion([Q0, Q1, Q2, Q3]), "scope" : qUnion([Q4])});
        }
        {
            var Q0;
            Q0=qCreatedBy(makeId("Right.planeOp"),FACE);
            var sketch = newSketch(context, id + "F8", { "sketchPlane" : qUnion([Q0])});
            skLineSegment(sketch, "E22", {"start": v(0, 0) * mm, "end": v(0, 50.68) * mm});
            skSolve(sketch);
        }
    });
